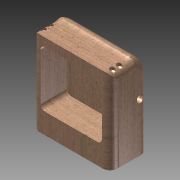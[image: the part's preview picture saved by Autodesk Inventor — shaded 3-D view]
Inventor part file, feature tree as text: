
AUTODESK INVENTOR PART (.ipt)
format: ipt  version: 2015 (Build 190159000, 159)  size: 320,000 bytes
history: native  units: in
note: dims shown in document units (in); Inventor stores cm internally (conversion verified against a paired STEP export)
features: sketch x5, extrude x5, fillet x4, hole x2, mirror x1
ambient origin geometry x8: Origin, YZ Plane, XZ Plane, XY Plane, X Axis, Y Axis, Z Axis, Center Point
bodies: Solid1 (feature_tree)
feature tree (17):
  sketch  "Sketch1"  dims[d0=3.17in d1=1.53in]
  extrude  "Extrusion1"  Depth=1.53in
  extrude  "Extrusion5"  Depth=0.2in
  extrude  "Extrusion3"  Depth=1.0in
  extrude  "Extrusion4"  Depth=0.837in
  extrude  "Extrusion6"  Depth=2.5in
  fillet  "Fillet1"  Radius=1.07in
  fillet  "Fillet2"  Radius=0.06in
  fillet  "Fillet3"  Radius=0.3in
  hole  "Hole1"  [1 undecoded]
  hole  "Hole2"  [1 undecoded]
  mirror  "Mirror1"
  fillet  "Fillet4"  Radius=0.75in
  sketch  "Sketch3"  dims[d2=3.5in d3=0.0in d9=0.2in]
  sketch  "Sketch4"  dims[d10=2.5in d11=1.0in]
  sketch  "Sketch5"  dims[d12=0.57in d13=0.0in d15=0.837in]
  sketch  "Sketch6"  dims[d16=2.28in d17=2.5in d18=1.07in d19=0.0in d20=0.06in d21=0.3in d23=3.0in d24=0.0in d25=0.05in d26=0.75in d27=0.983in d28=3.0in d29=0.0in d30=0.75in d31=0.3in d32=0.3in d33=0.1in d34=0.28in d35=0.28in d36=2.8in d37=0.2in d38=0.75in d39=0.375in d40=0.25in d41=0.5635in d42=0.125in d43=0.8108in d44=2.0in d45=0.3in d46=0.29in d47=0.75in d48=0.375in d49=0.25in d50=0.5635in d51=0.35in d52=0.8108in d53=0.01in]
note: 2 required parameter values undecoded (feature->parameter linkage not recoverable at this tier; creation-order binding heuristic only, values carry confidence <= 0.55)
